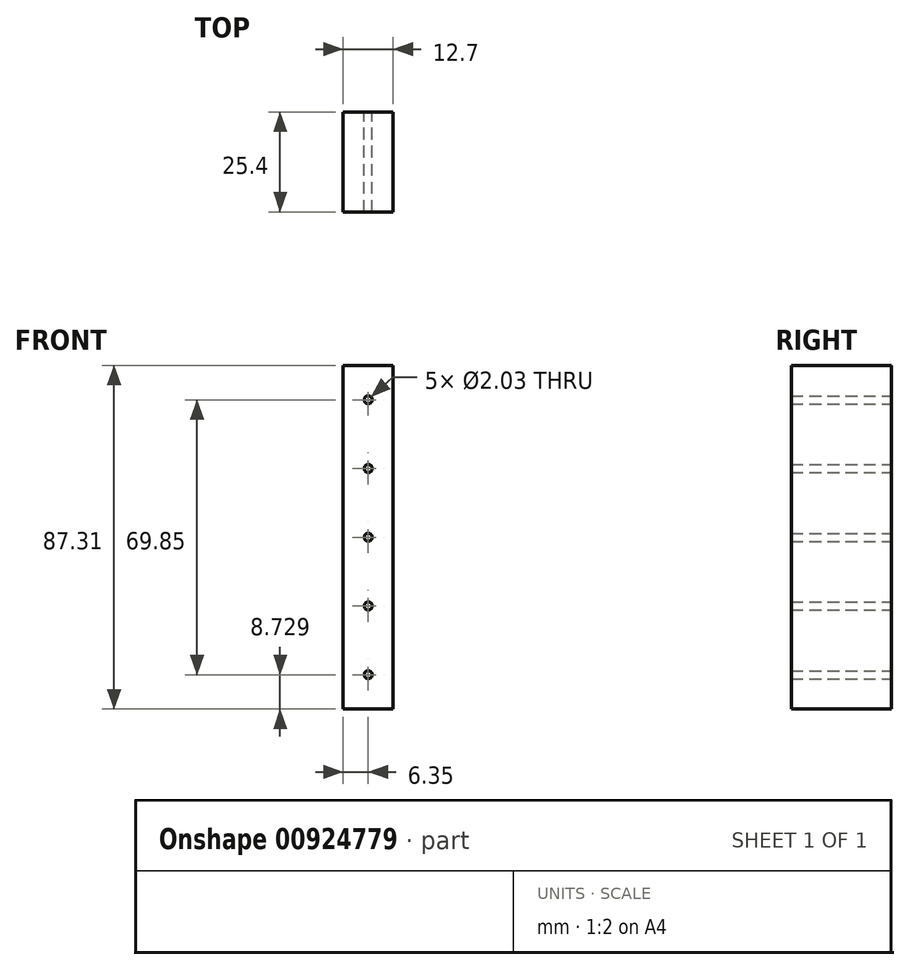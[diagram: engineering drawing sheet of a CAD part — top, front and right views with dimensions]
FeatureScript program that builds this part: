
annotation { "Feature Type Name" : "Feature", "Feature Type Description" : "" }
export const myFeature = defineFeature(function(context is Context, id is Id, definition is map)
    precondition{}
    {
        {
            var Q0;
            Q0=qCreatedBy(makeId("Front.planeOp"),FACE);
            var sketch = newSketch(context, id + "F0", { "sketchPlane" : qUnion([Q0])});
            skLineSegment(sketch, "E0", {"start": v(0, 0) * mm, "end": v(0, -87.31) * mm});
            skLineSegment(sketch, "E1", {"start": v(0, 0) * mm, "end": v(12.7, 0) * mm});
            skLineSegment(sketch, "E2", {"start": v(12.7, 0) * mm, "end": v(12.7, -87.31) * mm});
            skLineSegment(sketch, "E3", {"start": v(12.7, -87.31) * mm, "end": v(0, -87.31) * mm});
            skLineSegment(sketch, "E4", {"start": v(6.35, 0) * mm, "end": v(6.35, -87.31) * mm, "construction": true});
            skCircle(sketch, "E5", {"center": v(6.35, -8.73) * mm, "radius": 1.02 * mm});
            skCircle(sketch, "E6", {"center": v(6.35, -26.2) * mm, "radius": 1.02 * mm});
            skCircle(sketch, "E7", {"center": v(6.35, -43.66) * mm, "radius": 1.02 * mm});
            skCircle(sketch, "E8", {"center": v(6.35, -61.12) * mm, "radius": 1.02 * mm});
            skCircle(sketch, "E9", {"center": v(6.35, -78.58) * mm, "radius": 1.02 * mm});
            skSolve(sketch);
        }
        {
            var Q0;
            Q0=makeQuery(id+"F0.imprint","IMPRINT",FACE,{"disambiguationData":[TD([[makeQuery(id+"F0.imprint","IMPRINT",EDGE,{"derivedFrom":sQuery(id+"F0.wireOp",EDGE,"E0")}),1.0]])]});
            extrude(context, id + "F1", {"entities" : qUnion([Q0]), "depth" : 25.4 * mm, "offsetDistance" : 25.4 * mm});
        }
    });
